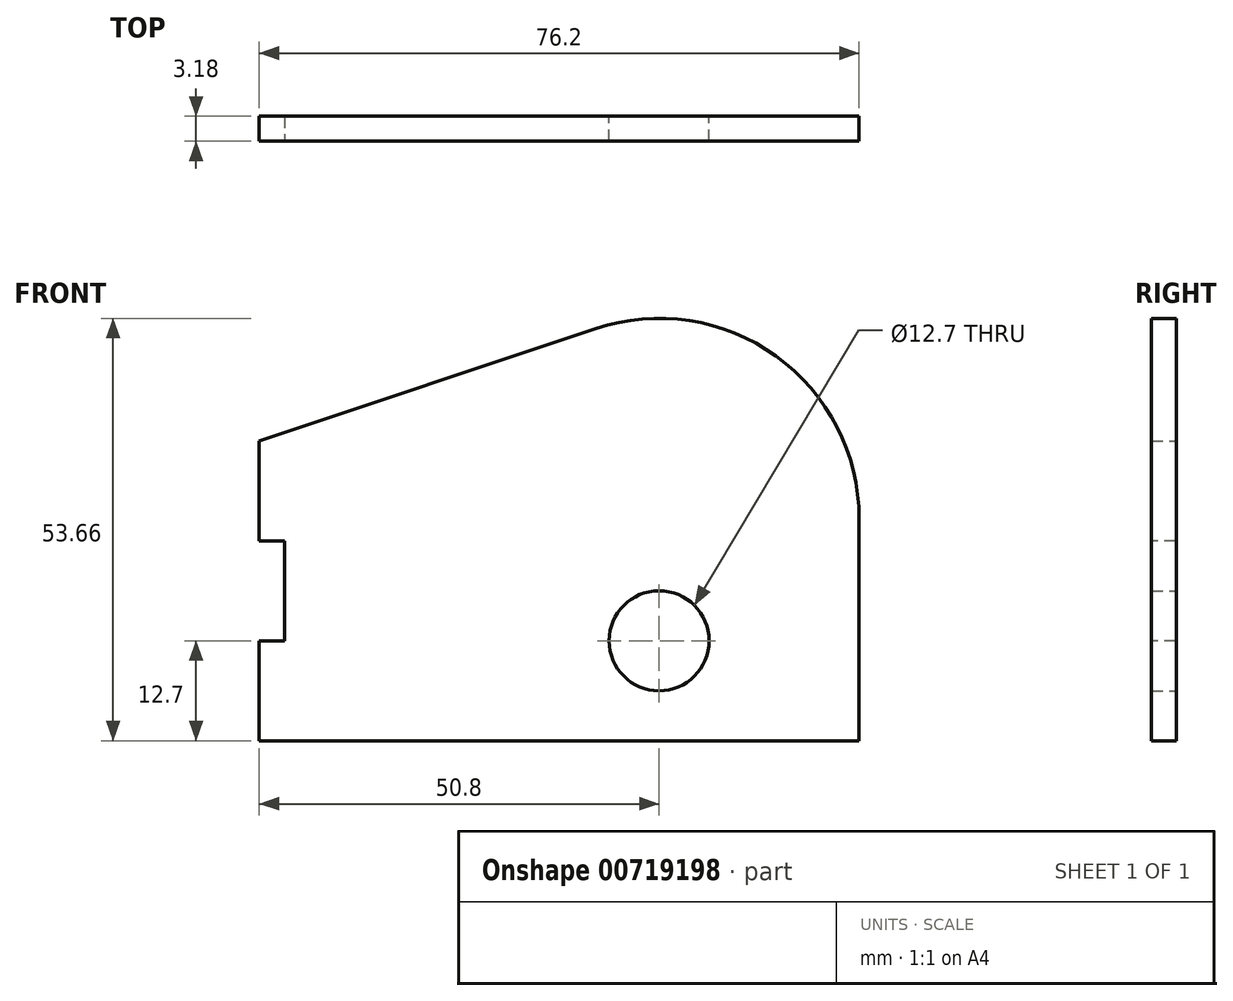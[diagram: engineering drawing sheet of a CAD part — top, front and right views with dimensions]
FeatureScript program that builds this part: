
annotation { "Feature Type Name" : "Feature", "Feature Type Description" : "" }
export const myFeature = defineFeature(function(context is Context, id is Id, definition is map)
    precondition{}
    {
        {
            var Q0;
            Q0=qCreatedBy(makeId("Front.planeOp"),FACE);
            var sketch = newSketch(context, id + "F0", { "sketchPlane" : qUnion([Q0])});
            skLineSegment(sketch, "E0", {"start": v(0, 0) * mm, "end": v(76.2, 0) * mm});
            skLineSegment(sketch, "E1", {"start": v(76.2, 0) * mm, "end": v(76.2, 28.26) * mm});
            skLineSegment(sketch, "E2", {"start": v(42.77, 52.36) * mm, "end": v(0, 38.1) * mm});
            skLineSegment(sketch, "E3", {"start": v(0, 38.1) * mm, "end": v(0, 0) * mm});
            skPoint(sketch, "E4.visualSharp", {"position": v(76.2, 63.5) * mm});
            skArc(sketch, "E4.filletArc", {"start": v(76.2, 28.26) * mm, "mid": v(65.65, 48.86) * mm, "end": v(42.77, 52.36) * mm});
            skCircle(sketch, "E5", {"center": v(50.8, 12.7) * mm, "radius": 6.35 * mm});
            skSolve(sketch);
        }
        {
            var Q0;
            Q0=makeQuery(id+"F0.imprint","IMPRINT",FACE,{"disambiguationData":[TD([[makeQuery(id+"F0.imprint","IMPRINT",EDGE,{"derivedFrom":sQuery(id+"F0.wireOp",EDGE,"E0")}),1.0]])]});
            extrude(context, id + "F1", {"entities" : qUnion([Q0]), "depth" : 3.17 * mm, "offsetDistance" : 25.4 * mm});
        }
        {
            var Q0;
            Q0=makeQuery(id+"F1.opExtrude","CAP_FACE",FACE,{"disambiguationData":[OSD([sQuery(id+"F0.wireOp",EDGE,"E0"),sQuery(id+"F0.wireOp",EDGE,"E1"),sQuery(id+"F0.wireOp",EDGE,"E2"),sQuery(id+"F0.wireOp",EDGE,"E3"),sQuery(id+"F0.wireOp",EDGE,"E4.filletArc"),sQuery(id+"F0.wireOp",EDGE,"E5")])],"isStart":false});
            var sketch = newSketch(context, id + "F2", { "sketchPlane" : qUnion([Q0])});
            skLineSegment(sketch, "E6.bottom", {"start": v(0, 25.4) * mm, "end": v(3.23, 25.4) * mm});
            skLineSegment(sketch, "E6.top", {"start": v(0, 12.7) * mm, "end": v(3.23, 12.7) * mm});
            skLineSegment(sketch, "E6.left", {"start": v(0, 25.4) * mm, "end": v(0, 12.7) * mm});
            skLineSegment(sketch, "E6.right", {"start": v(3.23, 25.4) * mm, "end": v(3.23, 12.7) * mm});
            skLineSegment(sketch, "E7", {"start": v(0, 38.1) * mm, "end": v(0, 25.4) * mm, "construction": true});
            skLineSegment(sketch, "E8", {"start": v(0, 12.7) * mm, "end": v(0, 0) * mm, "construction": true});
            skSolve(sketch);
        }
        {
            var Q0;
            Q0=makeQuery(id+"F2.imprint","IMPRINT",FACE,{"disambiguationData":[TD([[makeQuery(id+"F2.imprint","IMPRINT",EDGE,{"derivedFrom":sQuery(id+"F2.wireOp",EDGE,"E6.bottom")}),-1.0]])]});
            extrude(context, id + "F3", {"entities" : qUnion([Q0]), "operationType" : NewBodyOperationType.REMOVE, "oppositeDirection" : true, "depth" : 3.17 * mm, "offsetDistance" : 25.4 * mm});
        }
    });
